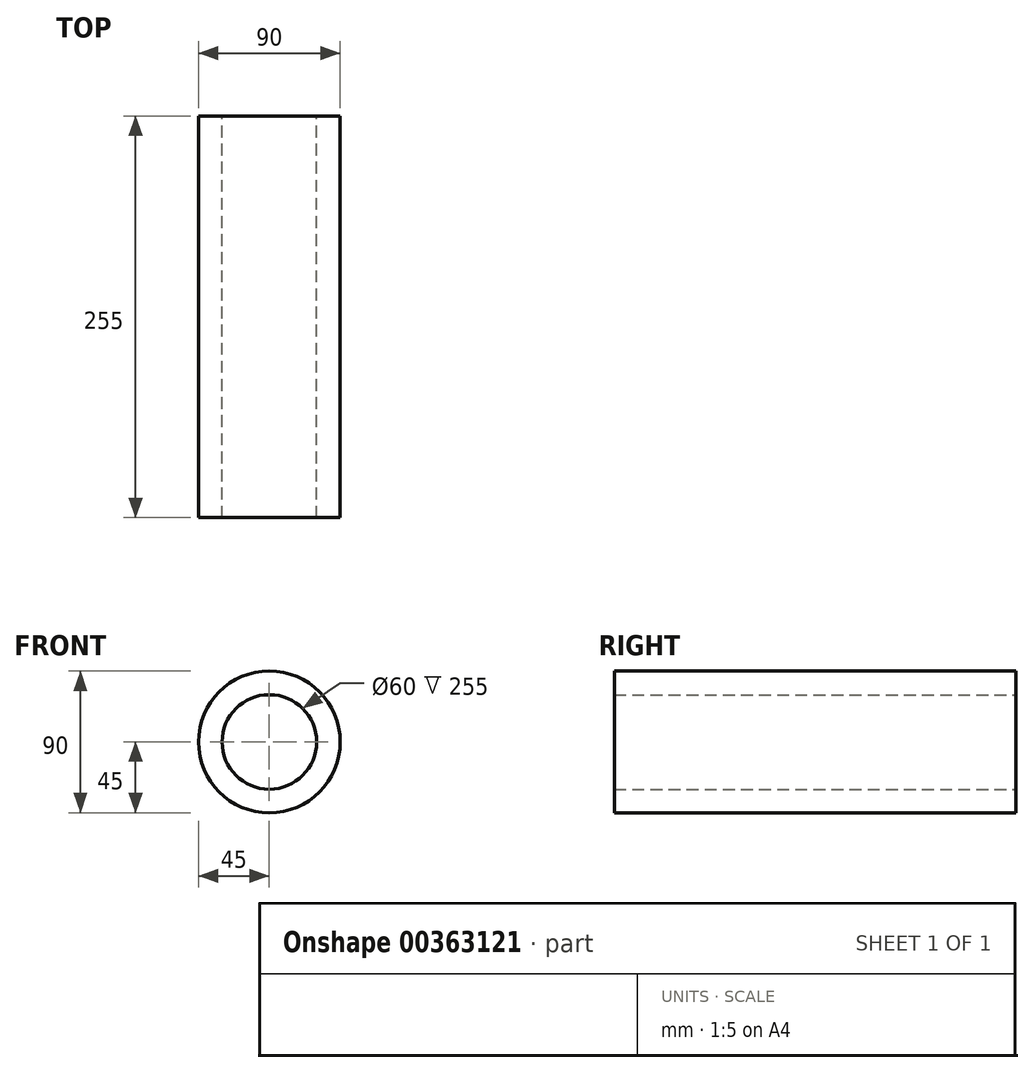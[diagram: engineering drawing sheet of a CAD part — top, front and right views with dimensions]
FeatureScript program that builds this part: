
annotation { "Feature Type Name" : "Feature", "Feature Type Description" : "" }
export const myFeature = defineFeature(function(context is Context, id is Id, definition is map)
    precondition{}
    {
        {
            var Q0;
            Q0=qCreatedBy(makeId("Front.planeOp"),FACE);
            var sketch = newSketch(context, id + "F0", { "sketchPlane" : qUnion([Q0])});
            skCircle(sketch, "E0", {"center": v(0, 0) * mm, "radius": 45 * mm});
            skCircle(sketch, "E1", {"center": v(0, 0) * mm, "radius": 30 * mm});
            skSolve(sketch);
        }
        {
            var Q0;
            Q0 = qSketchRegion(id + "F0", true);
            extrude(context, id + "F1", {"entities" : qUnion([Q0]), "depth" : 255 * mm});
        }
    });
